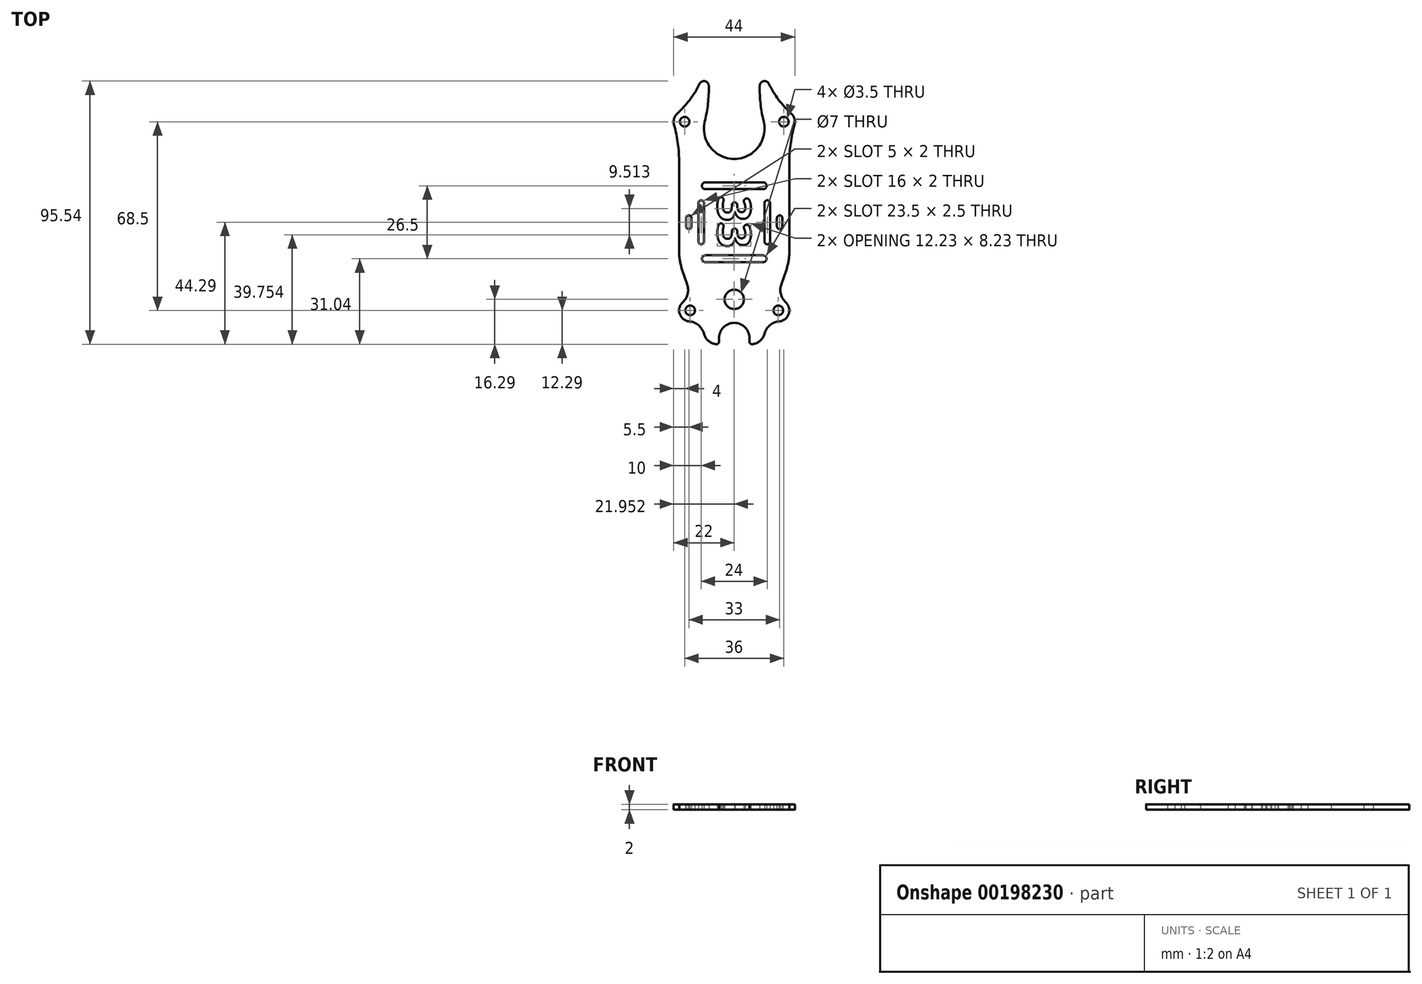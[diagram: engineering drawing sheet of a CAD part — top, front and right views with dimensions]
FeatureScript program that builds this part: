
annotation { "Feature Type Name" : "Feature", "Feature Type Description" : "" }
export const myFeature = defineFeature(function(context is Context, id is Id, definition is map)
    precondition{}
    {
        {
            var Q0;
            Q0=qCreatedBy(makeId("Top.planeOp"),FACE);
            var sketch = newSketch(context, id + "F0", { "sketchPlane" : qUnion([Q0])});
            skArc(sketch, "E0", {"start": v(-20.7, 39.46) * mm, "mid": v(-21.84, 37.62) * mm, "end": v(-21.86, 35.44) * mm});
            skLineSegment(sketch, "E1", {"start": v(-18.93, -17.14) * mm, "end": v(-17.05, -22.66) * mm});
            skArc(sketch, "E2", {"start": v(-10.68, 36.62) * mm, "mid": v(-8.66, 27.21) * mm, "end": v(0, 23) * mm});
            skLineSegment(sketch, "E3", {"start": v(0, 23) * mm, "end": v(0, -60) * mm, "construction": true});
            skCircle(sketch, "E4", {"center": v(-16, -32) * mm, "radius": 1.75 * mm});
            skArc(sketch, "E5.MirrorCS", {"start": v(10.68, 36.62) * mm, "mid": v(8.66, 27.21) * mm, "end": v(0, 23) * mm});
            skArc(sketch, "E6.MirrorCS", {"start": v(20.7, 39.46) * mm, "mid": v(21.84, 37.62) * mm, "end": v(21.86, 35.44) * mm});
            skCircle(sketch, "E7.MirrorC", {"center": v(16, -32) * mm, "radius": 1.75 * mm});
            skLineSegment(sketch, "E8.MirrorCS", {"start": v(18.93, -17.14) * mm, "end": v(17.05, -22.66) * mm});
            skCircle(sketch, "E9", {"center": v(-18, 36.5) * mm, "radius": 1.75 * mm});
            skCircle(sketch, "E10.MirrorC", {"center": v(18, 36.5) * mm, "radius": 1.75 * mm});
            skCircle(sketch, "E11", {"center": v(0, -28) * mm, "radius": 3.5 * mm});
            skArc(sketch, "E12", {"start": v(-7.28, -44.13) * mm, "mid": v(-7, -44.2) * mm, "end": v(-6.72, -44.26) * mm});
            skLineSegment(sketch, "E13.trimOffspring", {"start": v(-20, 21.67) * mm, "end": v(-20, -10.69) * mm});
            skArc(sketch, "E14", {"start": v(16.32, -35.99) * mm, "mid": v(19.79, -33.3) * mm, "end": v(18.7, -29.04) * mm});
            skArc(sketch, "E15.filletArc", {"start": v(16.32, -35.99) * mm, "mid": v(13.12, -37.23) * mm, "end": v(11.13, -40.03) * mm});
            skArc(sketch, "E16.filletArc", {"start": v(17.05, -22.66) * mm, "mid": v(16.92, -26.1) * mm, "end": v(18.7, -29.04) * mm});
            skArc(sketch, "E17.MirrorCS", {"start": v(-16.32, -35.99) * mm, "mid": v(-13.12, -37.23) * mm, "end": v(-11.13, -40.03) * mm});
            skArc(sketch, "E18.MirrorCS", {"start": v(-16.32, -35.99) * mm, "mid": v(-19.79, -33.3) * mm, "end": v(-18.7, -29.04) * mm});
            skArc(sketch, "E19.MirrorCS", {"start": v(-17.05, -22.66) * mm, "mid": v(-16.92, -26.1) * mm, "end": v(-18.7, -29.04) * mm});
            skText(sketch, "E20", { "text": "33", "fontName": "OpenSans-Bold.ttf"});
            skLineSegment(sketch, "E21", {"start": v(-11.13, -40.03) * mm, "end": v(-10.84, -40.89) * mm});
            skLineSegment(sketch, "E22", {"start": v(11.13, -40.03) * mm, "end": v(10.84, -40.89) * mm});
            skLineSegment(sketch, "E23", {"start": v(-17.05, -22.66) * mm, "end": v(-11.13, -40.03) * mm, "construction": true});
            skLineSegment(sketch, "E24", {"start": v(17.05, -22.66) * mm, "end": v(11.13, -40.03) * mm, "construction": true});
            skArc(sketch, "E25", {"start": v(-9.25, 49.53) * mm, "mid": v(-10.62, 51.2) * mm, "end": v(-12.57, 50.27) * mm});
            skArc(sketch, "E26", {"start": v(-20.7, 39.46) * mm, "mid": v(-16.12, 44.48) * mm, "end": v(-12.57, 50.27) * mm});
            skArc(sketch, "E27.MirrorCS", {"start": v(9.25, 49.53) * mm, "mid": v(10.62, 51.2) * mm, "end": v(12.57, 50.27) * mm});
            skArc(sketch, "E28.MirrorCS", {"start": v(20.7, 39.46) * mm, "mid": v(16.12, 44.48) * mm, "end": v(12.57, 50.27) * mm});
            skPoint(sketch, "E29.visualSharp", {"position": v(-10, -43.34) * mm});
            skArc(sketch, "E29.filletArc", {"start": v(-10.84, -40.89) * mm, "mid": v(-9.47, -42.97) * mm, "end": v(-7.28, -44.13) * mm});
            skPoint(sketch, "E30.visualSharp", {"position": v(10, -43.34) * mm});
            skArc(sketch, "E30.filletArc", {"start": v(7.28, -44.13) * mm, "mid": v(9.47, -42.97) * mm, "end": v(10.84, -40.89) * mm});
            skLineSegment(sketch, "E31", {"start": v(-16.5, 1.5) * mm, "end": v(-16.5, -1.5) * mm, "construction": true});
            skArc(sketch, "E32.0.startCap", {"start": v(-17.5, 1.5) * mm, "mid": v(-16.5, 2.5) * mm, "end": v(-15.5, 1.5) * mm});
            skArc(sketch, "E32.0.endCap", {"start": v(-15.5, -1.5) * mm, "mid": v(-16.5, -2.5) * mm, "end": v(-17.5, -1.5) * mm});
            skLineSegment(sketch, "E32.0.left", {"start": v(-15.5, 1.5) * mm, "end": v(-15.5, -1.5) * mm});
            skLineSegment(sketch, "E32.0.right", {"start": v(-17.5, 1.5) * mm, "end": v(-17.5, -1.5) * mm});
            skLineSegment(sketch, "E33.MirrorCS", {"start": v(16.5, 1.5) * mm, "end": v(16.5, -1.5) * mm, "construction": true});
            skLineSegment(sketch, "E34.MirrorCS", {"start": v(15.5, 1.5) * mm, "end": v(15.5, -1.5) * mm});
            skLineSegment(sketch, "E35.MirrorCS", {"start": v(17.5, 1.5) * mm, "end": v(17.5, -1.5) * mm});
            skArc(sketch, "E36.MirrorCS", {"start": v(17.5, 1.5) * mm, "mid": v(16.5, 2.5) * mm, "end": v(15.5, 1.5) * mm});
            skArc(sketch, "E37.MirrorCS", {"start": v(15.5, -1.5) * mm, "mid": v(16.5, -2.5) * mm, "end": v(17.5, -1.5) * mm});
            skArc(sketch, "E38.filletArc", {"start": v(-10.68, 36.62) * mm, "mid": v(-9.55, 43.03) * mm, "end": v(-9.25, 49.53) * mm});
            skArc(sketch, "E39.filletArc", {"start": v(9.25, 49.53) * mm, "mid": v(9.55, 43.03) * mm, "end": v(10.68, 36.62) * mm});
            skArc(sketch, "E40", {"start": v(-20, 21.67) * mm, "mid": v(-20.47, 28.62) * mm, "end": v(-21.86, 35.44) * mm});
            skArc(sketch, "E41.MirrorCS", {"start": v(20, 21.67) * mm, "mid": v(20.47, 28.62) * mm, "end": v(21.86, 35.44) * mm});
            skCircle(sketch, "E42", {"center": v(0, -28) * mm, "radius": 6 * mm, "construction": true});
            skLineSegment(sketch, "E43", {"start": v(20, 21.67) * mm, "end": v(20, -10.69) * mm});
            skLineSegment(sketch, "E44", {"start": v(-10.5, 13.25) * mm, "end": v(10.5, 13.25) * mm, "construction": true});
            skLineSegment(sketch, "E45", {"start": v(-10.5, -13.25) * mm, "end": v(10.5, -13.25) * mm, "construction": true});
            skArc(sketch, "E46.0.startCap", {"start": v(-10.5, 12) * mm, "mid": v(-11.75, 13.25) * mm, "end": v(-10.5, 14.5) * mm});
            skArc(sketch, "E46.0.endCap", {"start": v(10.5, 14.5) * mm, "mid": v(11.75, 13.25) * mm, "end": v(10.5, 12) * mm});
            skLineSegment(sketch, "E46.0.left", {"start": v(-10.5, 14.5) * mm, "end": v(10.5, 14.5) * mm});
            skLineSegment(sketch, "E46.0.right", {"start": v(-10.5, 12) * mm, "end": v(10.5, 12) * mm});
            skArc(sketch, "E46.1.startCap", {"start": v(-10.5, -14.5) * mm, "mid": v(-11.75, -13.25) * mm, "end": v(-10.5, -12) * mm});
            skArc(sketch, "E46.1.endCap", {"start": v(10.5, -12) * mm, "mid": v(11.75, -13.25) * mm, "end": v(10.5, -14.5) * mm});
            skLineSegment(sketch, "E46.1.left", {"start": v(-10.5, -12) * mm, "end": v(10.5, -12) * mm});
            skLineSegment(sketch, "E46.1.right", {"start": v(-10.5, -14.5) * mm, "end": v(10.5, -14.5) * mm});
            skPoint(sketch, "E47.visualSharp", {"position": v(-20, -14) * mm});
            skArc(sketch, "E47.filletArc", {"start": v(-20, -10.69) * mm, "mid": v(-19.73, -13.96) * mm, "end": v(-18.93, -17.14) * mm});
            skPoint(sketch, "E48.visualSharp", {"position": v(20, -14) * mm});
            skArc(sketch, "E48.filletArc", {"start": v(18.93, -17.14) * mm, "mid": v(19.73, -13.96) * mm, "end": v(20, -10.69) * mm});
            skLineSegment(sketch, "E49", {"start": v(-12, 7) * mm, "end": v(-12, -7) * mm, "construction": true});
            skLineSegment(sketch, "E50.MirrorCS", {"start": v(12, 7) * mm, "end": v(12, -7) * mm, "construction": true});
            skArc(sketch, "E51.0.startCap", {"start": v(-13, 7) * mm, "mid": v(-12, 8) * mm, "end": v(-11, 7) * mm});
            skArc(sketch, "E51.0.endCap", {"start": v(-11, -7) * mm, "mid": v(-12, -8) * mm, "end": v(-13, -7) * mm});
            skLineSegment(sketch, "E51.0.left", {"start": v(-11, 7) * mm, "end": v(-11, -7) * mm});
            skLineSegment(sketch, "E51.0.right", {"start": v(-13, 7) * mm, "end": v(-13, -7) * mm});
            skArc(sketch, "E51.3.startCap", {"start": v(11, 7) * mm, "mid": v(12, 8) * mm, "end": v(13, 7) * mm});
            skArc(sketch, "E51.3.endCap", {"start": v(13, -7) * mm, "mid": v(12, -8) * mm, "end": v(11, -7) * mm});
            skLineSegment(sketch, "E51.3.left", {"start": v(13, 7) * mm, "end": v(13, -7) * mm});
            skLineSegment(sketch, "E51.3.right", {"start": v(11, 7) * mm, "end": v(11, -7) * mm});
            skPoint(sketch, "E52.startSnap0", {"position": v(-16.5, 2.5) * mm});
            skArc(sketch, "E53", {"start": v(5.5, -42) * mm, "mid": v(0, -36.5) * mm, "end": v(-5.5, -42) * mm});
            skArc(sketch, "E54.trimOffspring", {"start": v(6.72, -44.26) * mm, "mid": v(7, -44.2) * mm, "end": v(7.28, -44.13) * mm});
            skLineSegment(sketch, "E55", {"start": v(-5.5, -42) * mm, "end": v(-5.5, -43.29) * mm});
            skLineSegment(sketch, "E56", {"start": v(5.5, -42) * mm, "end": v(5.5, -43.29) * mm});
            skPoint(sketch, "E57.visualSharp", {"position": v(-5.5, -44.5) * mm});
            skArc(sketch, "E57.filletArc", {"start": v(-6.72, -44.26) * mm, "mid": v(-5.87, -44.07) * mm, "end": v(-5.5, -43.29) * mm});
            skPoint(sketch, "E58.visualSharp", {"position": v(5.5, -44.5) * mm});
            skArc(sketch, "E58.filletArc", {"start": v(5.5, -43.29) * mm, "mid": v(5.87, -44.07) * mm, "end": v(6.72, -44.26) * mm});
            const initialGuessF0  = {"E20": [-0.006, 0.00973, 0, -1, 0.012]};
            skSetInitialGuess(sketch, initialGuessF0);
            skSolve(sketch);
        }
        {
            var Q0;
            Q0=qSketchRegion(id+"F0",true);
            extrude(context, id + "F1", {"entities" : qUnion([Q0]), "depth" : 2 * mm});
        }
        {
            var Q0;
            Q0=makeQuery(id+"F1.opExtrude","SWEPT_EDGE",EDGE,{"disambiguationData":[OSD([sQuery(id+"F0.wireOp",EDGE,"E20.sketch_text.stroke-23"),sQuery(id+"F0.wireOp",EDGE,"E20.sketch_text.stroke-24")])]});
            var Q1;
            Q1=makeQuery(id+"F1.opExtrude","SWEPT_EDGE",EDGE,{"disambiguationData":[OSD([sQuery(id+"F0.wireOp",EDGE,"E20.sketch_text.stroke-22"),sQuery(id+"F0.wireOp",EDGE,"E20.sketch_text.stroke-23")])]});
            var Q2;
            Q2=makeQuery(id+"F1.opExtrude","SWEPT_EDGE",EDGE,{"disambiguationData":[OSD([sQuery(id+"F0.wireOp",EDGE,"E20.sketch_text.stroke-16"),sQuery(id+"F0.wireOp",EDGE,"E20.sketch_text.stroke-17")])]});
            var Q3;
            Q3=makeQuery(id+"F1.opExtrude","SWEPT_EDGE",EDGE,{"disambiguationData":[OSD([sQuery(id+"F0.wireOp",EDGE,"E20.sketch_text.stroke-15"),sQuery(id+"F0.wireOp",EDGE,"E20.sketch_text.stroke-16")])]});
            var Q4;
            Q4=makeQuery(id+"F1.opExtrude","SWEPT_EDGE",EDGE,{"disambiguationData":[OSD([sQuery(id+"F0.wireOp",EDGE,"E20.sketch_text.stroke-8"),sQuery(id+"F0.wireOp",EDGE,"E20.sketch_text.stroke-9")])]});
            var Q5;
            Q5=makeQuery(id+"F1.opExtrude","SWEPT_EDGE",EDGE,{"disambiguationData":[OSD([sQuery(id+"F0.wireOp",EDGE,"E20.sketch_text.stroke-7"),sQuery(id+"F0.wireOp",EDGE,"E20.sketch_text.stroke-8")])]});
            var Q6;
            Q6=makeQuery(id+"F1.opExtrude","SWEPT_EDGE",EDGE,{"disambiguationData":[OSD([sQuery(id+"F0.wireOp",EDGE,"E20.sketch_text.stroke-35"),sQuery(id+"F0.wireOp",EDGE,"E20.sketch_text.stroke-36")])]});
            var Q7;
            Q7=makeQuery(id+"F1.opExtrude","SWEPT_EDGE",EDGE,{"disambiguationData":[OSD([sQuery(id+"F0.wireOp",EDGE,"E20.sketch_text.stroke-34"),sQuery(id+"F0.wireOp",EDGE,"E20.sketch_text.stroke-35")])]});
            var Q8;
            Q8=makeQuery(id+"F1.opExtrude","SWEPT_EDGE",EDGE,{"disambiguationData":[OSD([sQuery(id+"F0.wireOp",EDGE,"E20.sketch_text.stroke-42"),sQuery(id+"F0.wireOp",EDGE,"E20.sketch_text.stroke-43")])]});
            var Q9;
            Q9=makeQuery(id+"F1.opExtrude","SWEPT_EDGE",EDGE,{"disambiguationData":[OSD([sQuery(id+"F0.wireOp",EDGE,"E20.sketch_text.stroke-43"),sQuery(id+"F0.wireOp",EDGE,"E20.sketch_text.stroke-44")])]});
            var Q10;
            Q10=makeQuery(id+"F1.opExtrude","SWEPT_EDGE",EDGE,{"disambiguationData":[OSD([sQuery(id+"F0.wireOp",EDGE,"E20.sketch_text.stroke-49"),sQuery(id+"F0.wireOp",EDGE,"E20.sketch_text.stroke-50")])]});
            var Q11;
            Q11=makeQuery(id+"F1.opExtrude","SWEPT_EDGE",EDGE,{"disambiguationData":[OSD([sQuery(id+"F0.wireOp",EDGE,"E20.sketch_text.stroke-50"),sQuery(id+"F0.wireOp",EDGE,"E20.sketch_text.stroke-51")])]});
            fillet(context, id + "F2", {"entities" : qUnion([Q0, Q1, Q2, Q3, Q4, Q5, Q6, Q7, Q8, Q9, Q10, Q11]), "radius" : 1 * mm, "tangentPropagation" : true, "allowEdgeOverflow" : false});
        }
    });
